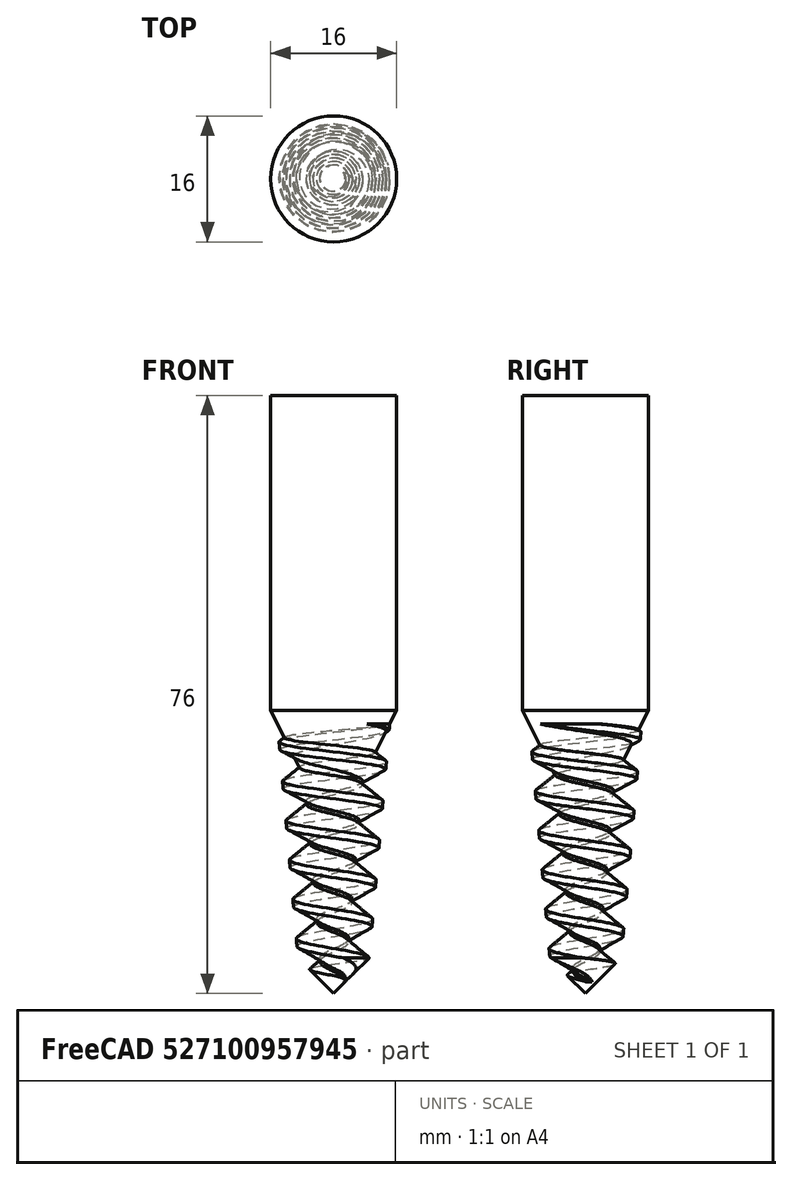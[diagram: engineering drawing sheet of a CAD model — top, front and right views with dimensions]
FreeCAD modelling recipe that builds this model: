
FCSTD DOCUMENT  (FreeCAD 0.16R6662 (Git))
Label: tapered-screw-1
License: CreativeCommons Attribution-ShareAlike
LicenseURL: http://creativecommons.org/licenses/by-sa/4.0/
objects: Part::Cone×3, Part::MultiFuse×2, Part::Helix×1, Sketcher::SketchObject×1, Part::Part2DObjectPython×1, Part::Sweep×1, Part::MultiCommon×1, Part::Cylinder×1
note: 11 computed .brp shape members not serialized (recipe doc carries the construction recipe); baked Part::Feature solids carry a one-line shape summary decoded from their .brp

FEATURE [Part::Helix] Helix001
  Angle = 5
  Height = 40
  LocalCoord = 1
  Pitch = 5
  Radius = 2.6
  Style = 1
FEATURE [Sketcher::SketchObject] Sketch
  Placement = pos=(0,0,10) rot=(1,0,0;1.5708rad)
  sketch-geometry (4):
    g0: LineSegment StartX=-12 StartY=0 StartZ=0 EndX=-9 EndY=-2 EndZ=0
    g1: LineSegment StartX=-9 StartY=-2 StartZ=0 EndX=-9 EndY=3 EndZ=0
    g2: LineSegment StartX=-9 StartY=3 StartZ=0 EndX=-12 EndY=1 EndZ=0
    g3: LineSegment StartX=-12 StartY=1 StartZ=0 EndX=-12 EndY=0 EndZ=0
  constraints (7):
    c: PointOnObject(g0,g-1)
    c: Coincident(g0,g1)
    c: Vertical(g1)
    c: Coincident(g2,g3)
    c: Coincident(g3,g0)
    c: Vertical(g3)
    c: Coincident(g1,g2)
FEATURE [Part::Part2DObjectPython] DWire  # Draft 2D object (typed FeaturePython)
  Base = -> Sketch
  ChamferSize = 0
  Closed = true
  End = (0.832728,0,-2.23493)
  FilletRadius = 0
  Length = 18.5084
  MakeFace = true
  Placement = pos=(-7,0,11.5) rot=(0,1,0;3.22886rad)
  Points = (7) [(-9,2.07761e-16,10.9357),(-11,0,10),(-9,-2.22045e-16,9),(-9,-6.66134e-16,7),(-7,-6.66134e-16,7),(-7,6.66134e-16,13),(-9,6.66134e-16,13)]
  Start = (1.01265,0,-0.178461)
  Subdivisions = 0
FEATURE [Part::Sweep] Sweep
  Frenet = true
  Sections = -> [DWire]
  Solid = true
  Spine = -> Helix001
  Transition = 1
FEATURE [Part::Cone] Cone
  Angle = 360
  Height = 46
  Placement = pos=(0,0,-3) rot=(0,0,1;0rad)
  Radius1 = 1
  Radius2 = 5
FEATURE [Part::MultiFuse] Fusion
  Shapes = -> [Sweep,Cone]
FEATURE [Part::Cone] Cone001
  Angle = 360
  Height = 50
  Placement = pos=(0,0,1) rot=(0,0,1;0rad)
  Radius1 = 0
  Radius2 = 50
FEATURE [Part::MultiCommon] Common
  Shapes = -> [Fusion,Cone001]
FEATURE [Part::Cone] Cone002
  Angle = 360
  Height = 10
  Placement = pos=(0,0,27) rot=(0,0,1;0rad)
  Radius1 = 3
  Radius2 = 8
FEATURE [Part::Cylinder] Cylinder
  Angle = 360
  Height = 40
  Placement = pos=(0,0,37) rot=(0,0,1;0rad)
  Radius = 8
FEATURE [Part::MultiFuse] Fusion001
  Shapes = -> [Cylinder,Cone002,Common]
